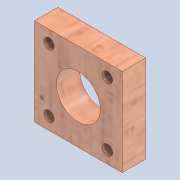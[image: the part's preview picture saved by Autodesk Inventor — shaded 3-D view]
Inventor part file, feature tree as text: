
AUTODESK INVENTOR PART (.ipt)
format: ipt  version: 2020 (Build 240168000, 168)  size: 180,736 bytes
history: native  units: mm
features: extrude x3, sketch x3
ambient origin geometry x8: Origin, YZ Plane, XZ Plane, XY Plane, X Axis, Y Axis, Z Axis, Center Point
bodies: Solid1 (feature_tree)
feature tree (6):
  extrude  "Extrusion1"  Depth=30.0mm
  extrude  "Extrusion2"  TaperAngle=0.0deg  [1 undecoded]
  extrude  "Extrusion3"  TaperAngle=0.0deg  [1 undecoded]
  sketch  "Sketch1"  dims[d0=30.0mm d1=30.0mm]
  sketch  "Sketch2"  dims[d2=8.0mm d3=0.0mm d6=0.0mm d7=0.0mm]
  sketch  "Sketch3"  dims[d9=3.5mm d15=0.0mm d16=0.0mm d17=15.0mm d19=10.75mm d20=10.75mm d21=20.0mm d22=21.5mm]
note: 2 required parameter values undecoded (feature->parameter linkage not recoverable at this tier; creation-order binding heuristic only, values carry confidence <= 0.55)
